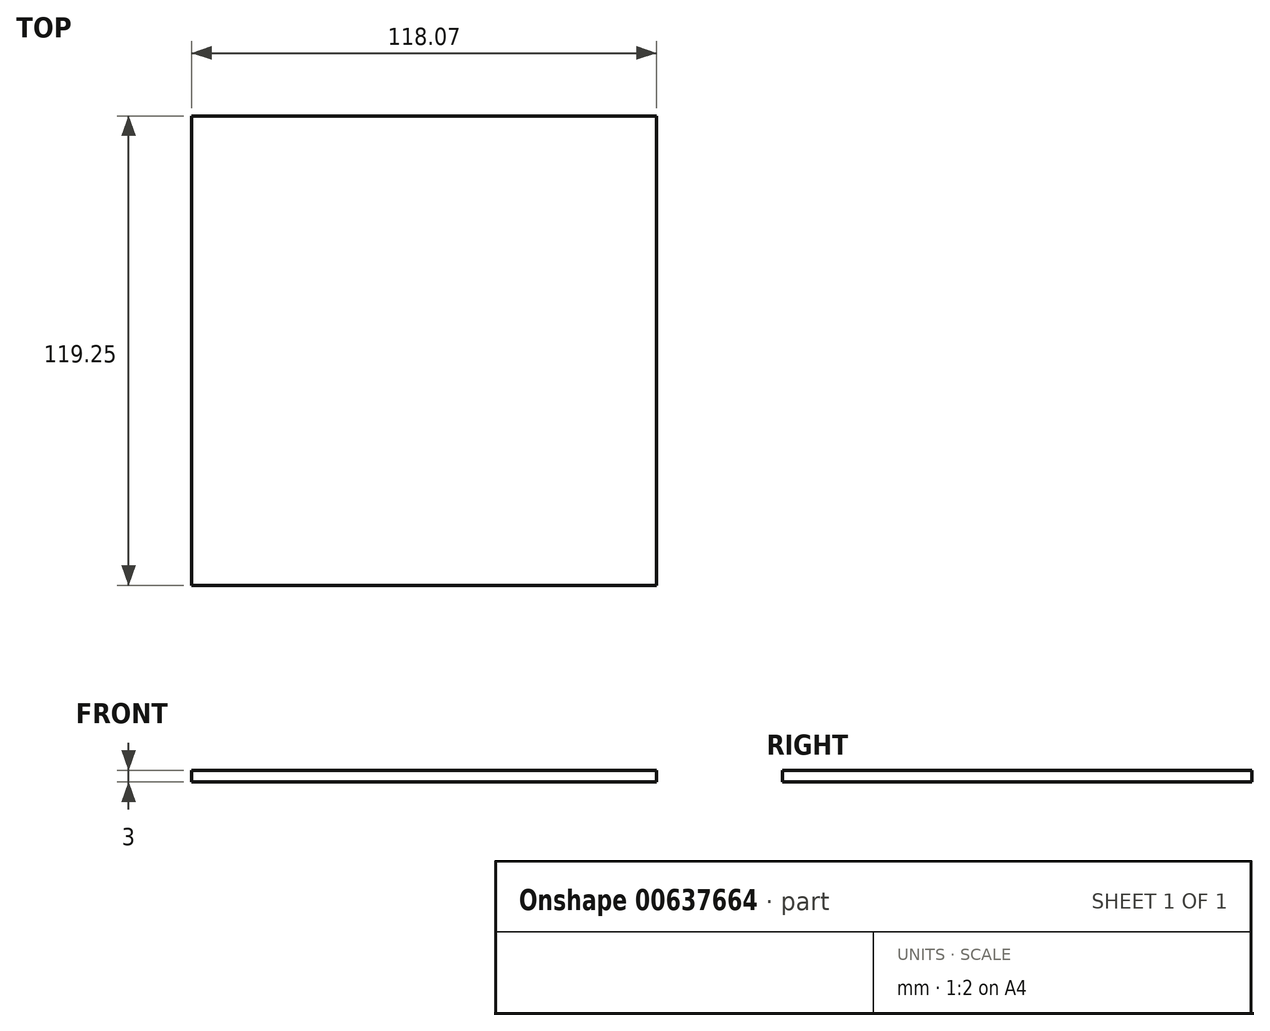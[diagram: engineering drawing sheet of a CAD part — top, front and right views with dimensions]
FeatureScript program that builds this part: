
annotation { "Feature Type Name" : "Feature", "Feature Type Description" : "" }
export const myFeature = defineFeature(function(context is Context, id is Id, definition is map)
    precondition{}
    {
        {
            var Q0;
            Q0=qCreatedBy(makeId("Top.planeOp"),FACE);
            var sketch = newSketch(context, id + "F0", { "sketchPlane" : qUnion([Q0])});
            skCircle(sketch, "E0.MirrorC", {"center": v(-28, 100.18) * mm, "radius": 1.65 * mm});
            skLineSegment(sketch, "E1.bottom", {"start": v(-57.12, 55.03) * mm, "end": v(60.95, 55.03) * mm});
            skLineSegment(sketch, "E1.top", {"start": v(-57.12, -64.22) * mm, "end": v(60.95, -64.22) * mm});
            skLineSegment(sketch, "E1.left", {"start": v(-57.12, 55.03) * mm, "end": v(-57.12, -64.22) * mm});
            skLineSegment(sketch, "E1.right", {"start": v(60.95, 55.03) * mm, "end": v(60.95, -64.22) * mm});
            skSolve(sketch);
        }
        {
            var Q0;
            Q0=makeQuery(id+"F0.imprint","IMPRINT",FACE,{"disambiguationData":[TD([[makeQuery(id+"F0.imprint","IMPRINT",EDGE,{"derivedFrom":sQuery(id+"F0.wireOp",EDGE,"E1.bottom")}),-1.0]])]});
            extrude(context, id + "F1", {"entities" : qUnion([Q0]), "depth" : 3 * mm, "offsetDistance" : 25 * mm});
        }
    });
